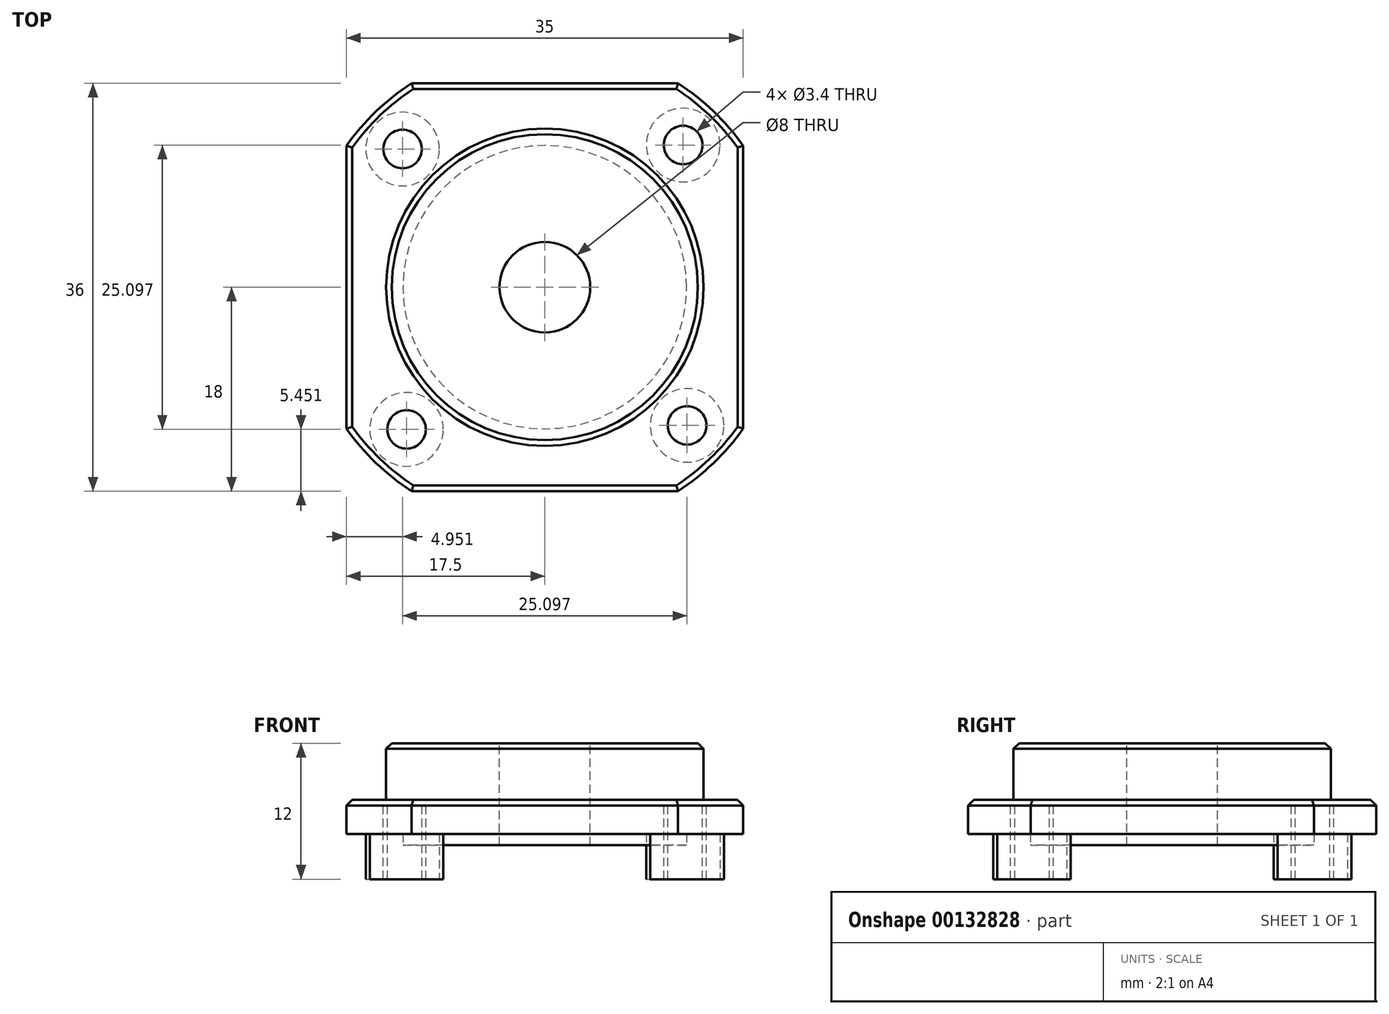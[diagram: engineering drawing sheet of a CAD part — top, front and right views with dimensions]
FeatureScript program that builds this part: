
annotation { "Feature Type Name" : "Feature", "Feature Type Description" : "" }
export const myFeature = defineFeature(function(context is Context, id is Id, definition is map)
    precondition{}
    {
        {
            var Q0;
            Q0=qCreatedBy(makeId("Top.planeOp"),FACE);
            var sketch = newSketch(context, id + "F0", { "sketchPlane" : qUnion([Q0])});
            skCircle(sketch, "E0", {"center": v(0, 0) * mm, "radius": 4 * mm});
            skLineSegment(sketch, "E1.bottom", {"start": v(17.5, 18) * mm, "end": v(-17.5, 18) * mm});
            skLineSegment(sketch, "E1.top", {"start": v(17.5, -18) * mm, "end": v(-17.5, -18) * mm});
            skLineSegment(sketch, "E1.left", {"start": v(17.5, 18) * mm, "end": v(17.5, -18) * mm});
            skLineSegment(sketch, "E1.right", {"start": v(-17.5, 18) * mm, "end": v(-17.5, -18) * mm});
            skCircle(sketch, "E2", {"center": v(0, 0) * mm, "radius": 21.5 * mm});
            skCircle(sketch, "E3", {"center": v(0, 0) * mm, "radius": 14 * mm});
            skCircle(sketch, "E4", {"center": v(0, 0) * mm, "radius": 17.5 * mm, "construction": true});
            skLineSegment(sketch, "E5", {"start": v(0, 0) * mm, "end": v(17.5, 18) * mm, "construction": true});
            skPoint(sketch, "E6", {"position": v(12.2, 12.55) * mm});
            skCircle(sketch, "E7", {"center": v(12.2, 12.55) * mm, "radius": 1.7 * mm});
            skCircle(sketch, "E8", {"center": v(12.2, 12.55) * mm, "radius": 3.25 * mm});
            skCircle(sketch, "E9.1.0", {"center": v(-12.55, 12.2) * mm, "radius": 1.7 * mm});
            skCircle(sketch, "E9.1.1", {"center": v(-12.55, 12.2) * mm, "radius": 3.25 * mm});
            skCircle(sketch, "E9.2.0", {"center": v(-12.2, -12.55) * mm, "radius": 1.7 * mm});
            skCircle(sketch, "E9.2.1", {"center": v(-12.2, -12.55) * mm, "radius": 3.25 * mm});
            skCircle(sketch, "E9.3.0", {"center": v(12.55, -12.2) * mm, "radius": 1.7 * mm});
            skCircle(sketch, "E9.3.1", {"center": v(12.55, -12.2) * mm, "radius": 3.25 * mm});
            skSolve(sketch);
        }
        {
            var Q0;
            Q0=makeQuery(id+"F0.imprint","IMPRINT",FACE,{"disambiguationData":[TD([[makeQuery(id+"F0.imprint","IMPRINT",EDGE,{"derivedFrom":sQuery(id+"F0.wireOp",EDGE,"E0")}),-1.0]])]});
            var Q1;
            Q1=makeQuery(id+"F0.imprint","IMPRINT",FACE,{"disambiguationData":[TD([[makeQuery(id+"F0.imprint","IMPRINT",EDGE,{"derivedFrom":sQuery(id+"F0.wireOp",EDGE,"E3")}),-1.0]])]});
            var Q2;
            Q2=makeQuery(id+"F0.imprint","IMPRINT",FACE,{"disambiguationData":[TD([[makeQuery(id+"F0.imprint","IMPRINT",EDGE,{"derivedFrom":sQuery(id+"F0.wireOp",EDGE,"E7")}),-1.0]])]});
            var Q3;
            Q3=makeQuery(id+"F0.imprint","IMPRINT",FACE,{"disambiguationData":[TD([[makeQuery(id+"F0.imprint","IMPRINT",EDGE,{"derivedFrom":sQuery(id+"F0.wireOp",EDGE,"E9.1.0")}),-1.0]])]});
            var Q4;
            Q4=makeQuery(id+"F0.imprint","IMPRINT",FACE,{"disambiguationData":[TD([[makeQuery(id+"F0.imprint","IMPRINT",EDGE,{"derivedFrom":sQuery(id+"F0.wireOp",EDGE,"E9.2.0")}),-1.0]])]});
            var Q5;
            Q5=makeQuery(id+"F0.imprint","IMPRINT",FACE,{"disambiguationData":[TD([[makeQuery(id+"F0.imprint","IMPRINT",EDGE,{"derivedFrom":sQuery(id+"F0.wireOp",EDGE,"E9.3.0")}),-1.0]])]});
            extrude(context, id + "F1", {"entities" : qUnion([Q0, Q1, Q2, Q3, Q4, Q5]), "oppositeDirection" : true, "depth" : 7 * mm});
        }
        {
            var Q0;
            Q0=makeQuery(id+"F0.imprint","IMPRINT",FACE,{"disambiguationData":[TD([[makeQuery(id+"F0.imprint","IMPRINT",EDGE,{"derivedFrom":sQuery(id+"F0.wireOp",EDGE,"E0")}),-1.0]])]});
            extrude(context, id + "F2", {"entities" : qUnion([Q0]), "operationType" : NewBodyOperationType.ADD, "depth" : 5 * mm});
        }
        {
            var Q0;
            Q0=makeQuery(id+"F1.opExtrude","CAP_FACE",FACE,{"disambiguationData":[OSD([sQuery(id+"F0.wireOp",EDGE,"E0"),sQuery(id+"F0.wireOp",EDGE,"E1.bottom"),sQuery(id+"F0.wireOp",EDGE,"E1.top"),sQuery(id+"F0.wireOp",EDGE,"E1.left"),sQuery(id+"F0.wireOp",EDGE,"E1.right"),sQuery(id+"F0.wireOp",EDGE,"E2"),sQuery(id+"F0.wireOp",EDGE,"E7"),sQuery(id+"F0.wireOp",EDGE,"E9.1.0"),sQuery(id+"F0.wireOp",EDGE,"E9.2.0"),sQuery(id+"F0.wireOp",EDGE,"E9.3.0")])],"isStart":false});
            var sketch = newSketch(context, id + "F3", { "sketchPlane" : qUnion([Q0])});
            skCircle(sketch, "E10.0", {"center": v(12.55, 12.2) * mm, "radius": 3.25 * mm});
            skCircle(sketch, "E10.1", {"center": v(12.2, -12.55) * mm, "radius": 3.25 * mm});
            skCircle(sketch, "E10.2", {"center": v(-12.55, -12.2) * mm, "radius": 3.25 * mm});
            skCircle(sketch, "E10.3", {"center": v(-12.2, 12.55) * mm, "radius": 3.25 * mm});
            skCircle(sketch, "E11", {"center": v(0, 0) * mm, "radius": 12.5 * mm});
            skSolve(sketch);
        }
        {
            var Q0;
            Q0=makeQuery(id+"F3.imprint","IMPRINT",FACE,{"disambiguationData":[TD([[makeQuery(id+"F3.imprint","IMPRINT",EDGE,{"derivedFrom":sQuery(id+"F3.wireOp",EDGE,"E10.3")}),-1.0]])]});
            var Q1;
            Q1=makeQuery(id+"F3.imprint","IMPRINT",FACE,{"disambiguationData":[TD([[makeQuery(id+"F3.imprint","IMPRINT",EDGE,{"derivedFrom":sQuery(id+"F3.wireOp",EDGE,"E10.0")}),-1.0]])]});
            var Q2;
            Q2=makeQuery(id+"F3.imprint","IMPRINT",FACE,{"disambiguationData":[TD([[makeQuery(id+"F3.imprint","IMPRINT",EDGE,{"derivedFrom":sQuery(id+"F3.wireOp",EDGE,"E10.1")}),-1.0]])]});
            var Q3;
            Q3=makeQuery(id+"F3.imprint","IMPRINT",FACE,{"disambiguationData":[TD([[makeQuery(id+"F3.imprint","IMPRINT",EDGE,{"derivedFrom":sQuery(id+"F3.wireOp",EDGE,"E10.2")}),-1.0]])]});
            extrude(context, id + "F4", {"entities" : qUnion([Q0, Q1, Q2, Q3]), "operationType" : NewBodyOperationType.REMOVE, "oppositeDirection" : true, "depth" : 4 * mm});
        }
        {
            var Q0;
            Q0=makeQuery(id+"F3.imprint","IMPRINT",FACE,{"disambiguationData":[TD([[makeQuery(id+"F3.imprint","IMPRINT",EDGE,{"derivedFrom":sQuery(id+"F3.wireOp",EDGE,"E11")}),1.0]])]});
            extrude(context, id + "F5", {"entities" : qUnion([Q0]), "operationType" : NewBodyOperationType.REMOVE, "oppositeDirection" : true, "depth" : 3 * mm});
        }
        {
            var Q0;
            Q0=makeQuery(id+"F1.opExtrude","CAP_EDGE",EDGE,{"disambiguationData":[OSD([sQuery(id+"F0.wireOp",EDGE,"E1.right")])],"isStart":true});
            var Q1;
            {var subQ0=sQuery(id+"F0.wireOp",EDGE,"E2");Q1=makeQuery(id+"F1.opExtrude","CAP_EDGE",EDGE,{"disambiguationData":[OSD([subQ0]),TDD([makeQuery(id+"F0.imprint","IMPRINT",EDGE,{"disambiguationData":[TD([[makeQuery(id+"F0.imprint","INTERSECT",VERTEX,{"disambiguationData":[OD(1.0)],"derivedFrom":[sQuery(id+"F0.wireOp",EDGE,"E1.top"),subQ0]}),1.0]])],"derivedFrom":subQ0})])],"isStart":true});}
            var Q2;
            Q2=makeQuery(id+"F1.opExtrude","CAP_EDGE",EDGE,{"disambiguationData":[OSD([sQuery(id+"F0.wireOp",EDGE,"E1.top")])],"isStart":false});
            var Q3;
            {var subQ0=sQuery(id+"F0.wireOp",EDGE,"E2");Q3=makeQuery(id+"F1.opExtrude","CAP_EDGE",EDGE,{"disambiguationData":[OSD([subQ0]),TDD([makeQuery(id+"F0.imprint","IMPRINT",EDGE,{"disambiguationData":[TD([[makeQuery(id+"F0.imprint","INTERSECT",VERTEX,{"disambiguationData":[OD(0.0)],"derivedFrom":[sQuery(id+"F0.wireOp",EDGE,"E1.top"),subQ0]}),-1.0]])],"derivedFrom":subQ0})])],"isStart":false});}
            var Q4;
            Q4=makeQuery(id+"F1.opExtrude","CAP_EDGE",EDGE,{"disambiguationData":[OSD([sQuery(id+"F0.wireOp",EDGE,"E1.left")])],"isStart":false});
            var Q5;
            {var subQ0=sQuery(id+"F0.wireOp",EDGE,"E2");Q5=makeQuery(id+"F1.opExtrude","CAP_EDGE",EDGE,{"disambiguationData":[OSD([subQ0]),TDD([makeQuery(id+"F0.imprint","IMPRINT",EDGE,{"disambiguationData":[TD([[makeQuery(id+"F0.imprint","INTERSECT",VERTEX,{"disambiguationData":[OD(0.0)],"derivedFrom":[sQuery(id+"F0.wireOp",EDGE,"E1.bottom"),subQ0]}),1.0]])],"derivedFrom":subQ0})])],"isStart":false});}
            var Q6;
            Q6=makeQuery(id+"F1.opExtrude","CAP_EDGE",EDGE,{"disambiguationData":[OSD([sQuery(id+"F0.wireOp",EDGE,"E1.bottom")])],"isStart":false});
            var Q7;
            {var subQ0=sQuery(id+"F0.wireOp",EDGE,"E2");Q7=makeQuery(id+"F1.opExtrude","CAP_EDGE",EDGE,{"disambiguationData":[OSD([subQ0]),TDD([makeQuery(id+"F0.imprint","IMPRINT",EDGE,{"disambiguationData":[TD([[makeQuery(id+"F0.imprint","INTERSECT",VERTEX,{"disambiguationData":[OD(1.0)],"derivedFrom":[sQuery(id+"F0.wireOp",EDGE,"E1.bottom"),subQ0]}),-1.0]])],"derivedFrom":subQ0})])],"isStart":true});}
            var Q8;
            Q8=makeQuery(id+"F5.boolean.opBoolean","COPY",EDGE,{"derivedFrom":makeQuery(id+"F5.opExtrude","CAP_EDGE",EDGE,{"disambiguationData":[OSD([sQuery(id+"F3.wireOp",EDGE,"E11")])],"isStart":true})});
            var Q9;
            Q9=makeQuery(id+"F2.opExtrude","CAP_EDGE",EDGE,{"disambiguationData":[OSD([sQuery(id+"F0.wireOp",EDGE,"E3")])],"isStart":false});
            var Q10;
            {var subQ0=sQuery(id+"F0.wireOp",EDGE,"E2");Q10=makeQuery(id+"F1.opExtrude","CAP_EDGE",EDGE,{"disambiguationData":[OSD([subQ0]),TDD([makeQuery(id+"F0.imprint","IMPRINT",EDGE,{"disambiguationData":[TD([[makeQuery(id+"F0.imprint","INTERSECT",VERTEX,{"disambiguationData":[OD(0.0)],"derivedFrom":[sQuery(id+"F0.wireOp",EDGE,"E1.bottom"),subQ0]}),1.0]])],"derivedFrom":subQ0})])],"isStart":true});}
            var Q11;
            Q11=makeQuery(id+"F1.opExtrude","CAP_EDGE",EDGE,{"disambiguationData":[OSD([sQuery(id+"F0.wireOp",EDGE,"E1.left")])],"isStart":true});
            var Q12;
            {var subQ0=sQuery(id+"F0.wireOp",EDGE,"E2");Q12=makeQuery(id+"F1.opExtrude","CAP_EDGE",EDGE,{"disambiguationData":[OSD([subQ0]),TDD([makeQuery(id+"F0.imprint","IMPRINT",EDGE,{"disambiguationData":[TD([[makeQuery(id+"F0.imprint","INTERSECT",VERTEX,{"disambiguationData":[OD(0.0)],"derivedFrom":[sQuery(id+"F0.wireOp",EDGE,"E1.top"),subQ0]}),-1.0]])],"derivedFrom":subQ0})])],"isStart":true});}
            var Q13;
            Q13=makeQuery(id+"F1.opExtrude","CAP_EDGE",EDGE,{"disambiguationData":[OSD([sQuery(id+"F0.wireOp",EDGE,"E1.top")])],"isStart":true});
            var Q14;
            Q14=makeQuery(id+"F1.opExtrude","CAP_EDGE",EDGE,{"disambiguationData":[OSD([sQuery(id+"F0.wireOp",EDGE,"E1.bottom")])],"isStart":true});
            chamfer(context, id + "F6", {"entities" : qUnion([Q0, Q1, Q2, Q3, Q4, Q5, Q6, Q7, Q8, Q9, Q10, Q11, Q12, Q13, Q14]), "width" : 0.5 * mm, "tangentPropagation" : true});
        }
    });
